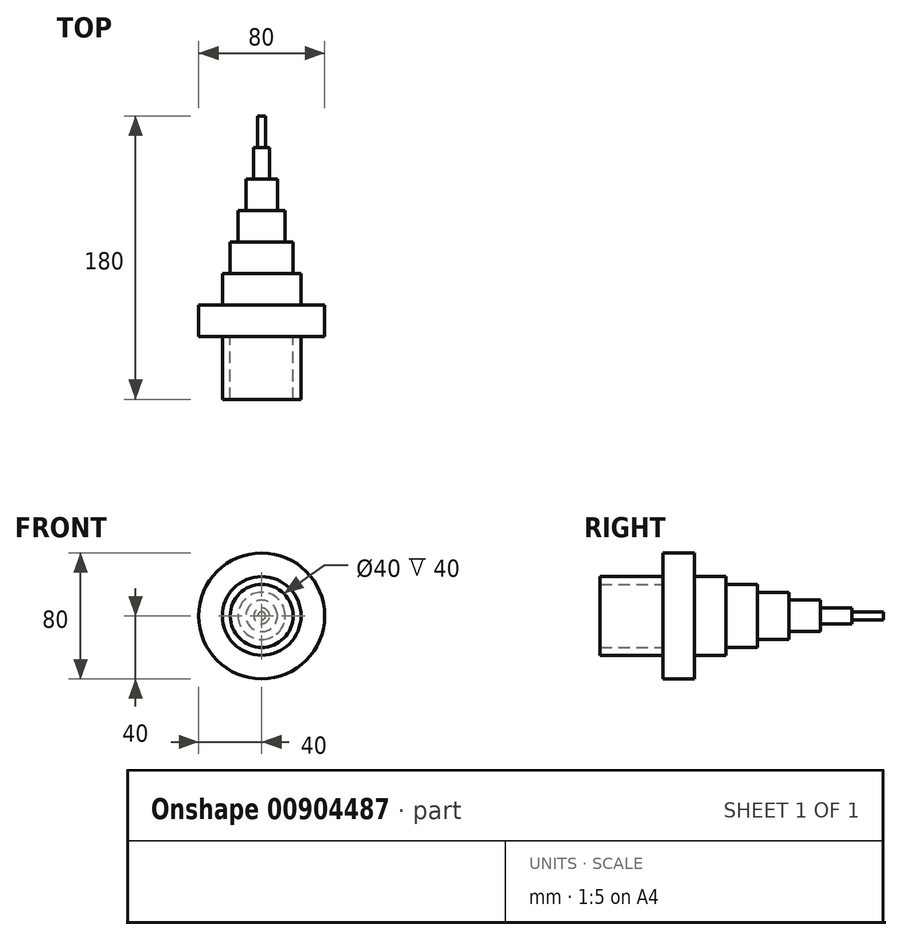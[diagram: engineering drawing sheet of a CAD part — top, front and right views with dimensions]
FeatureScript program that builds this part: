
annotation { "Feature Type Name" : "Feature", "Feature Type Description" : "" }
export const myFeature = defineFeature(function(context is Context, id is Id, definition is map)
    precondition{}
    {
        {
            var Q0;
            Q0=qCreatedBy(makeId("Front.planeOp"),FACE);
            var sketch = newSketch(context, id + "F0", { "sketchPlane" : qUnion([Q0])});
            skCircle(sketch, "E0", {"center": v(0, 0) * mm, "radius": 40 * mm});
            skSolve(sketch);
        }
        {
            var Q0;
            Q0=makeQuery(id+"F0.imprint","IMPRINT",FACE,{"disambiguationData":[TD([[makeQuery(id+"F0.imprint","IMPRINT",EDGE,{"derivedFrom":sQuery(id+"F0.wireOp",EDGE,"E0")}),1.0]])]});
            extrude(context, id + "F1", {"entities" : qUnion([Q0]), "depth" : 20 * mm, "offsetDistance" : 25.4 * mm});
        }
        {
            var Q0;
            Q0=makeQuery(id+"F1.opExtrude","CAP_FACE",FACE,{"disambiguationData":[OSD([sQuery(id+"F0.wireOp",EDGE,"E0")])],"isStart":false});
            var sketch = newSketch(context, id + "F2", { "sketchPlane" : qUnion([Q0])});
            skCircle(sketch, "E1", {"center": v(0, 0) * mm, "radius": 25 * mm});
            skCircle(sketch, "E2", {"center": v(0, 0) * mm, "radius": 20 * mm});
            skSolve(sketch);
        }
        {
            var Q0;
            Q0 = qSketchRegion(id + "F2", true);
            extrude(context, id + "F3", {"entities" : qUnion([Q0]), "operationType" : NewBodyOperationType.ADD, "depth" : 40 * mm, "offsetDistance" : 25.4 * mm});
        }
        {
            var Q0;
            Q0=makeQuery(id+"F1.opExtrude","CAP_FACE",FACE,{"disambiguationData":[OSD([sQuery(id+"F0.wireOp",EDGE,"E0")])],"isStart":true});
            var sketch = newSketch(context, id + "F4", { "sketchPlane" : qUnion([Q0])});
            skCircle(sketch, "E3", {"center": v(0, 0) * mm, "radius": 25 * mm});
            skCircle(sketch, "E4", {"center": v(0, 0) * mm, "radius": 20 * mm});
            skCircle(sketch, "E5", {"center": v(0, 0) * mm, "radius": 15 * mm});
            skCircle(sketch, "E6", {"center": v(0, 0) * mm, "radius": 10 * mm});
            skCircle(sketch, "E7", {"center": v(0, 0) * mm, "radius": 5 * mm});
            skCircle(sketch, "E8", {"center": v(0, 0) * mm, "radius": 2.5 * mm});
            skSolve(sketch);
        }
        {
            var Q0;
            Q0=makeQuery(id+"F4.imprint","IMPRINT",FACE,{"disambiguationData":[TD([[makeQuery(id+"F4.imprint","IMPRINT",EDGE,{"derivedFrom":sQuery(id+"F4.wireOp",EDGE,"E3")}),1.0]])]});
            extrude(context, id + "F5", {"entities" : qUnion([Q0]), "operationType" : NewBodyOperationType.ADD, "depth" : 20 * mm, "offsetDistance" : 25.4 * mm});
        }
        {
            var Q0;
            Q0=makeQuery(id+"F5.boolean.opBoolean","SPLIT",FACE,{"disambiguationData":[TD([makeQuery(id+"F5.opExtrude","SWEPT_FACE",FACE,{"disambiguationData":[OSD([sQuery(id+"F4.wireOp",EDGE,"E4")])]})])],"derivedFrom":makeQuery(id+"F1.opExtrude","CAP_FACE",FACE,{"disambiguationData":[OSD([sQuery(id+"F0.wireOp",EDGE,"E0")])],"isStart":true})});
            extrude(context, id + "F6", {"entities" : qUnion([Q0]), "operationType" : NewBodyOperationType.ADD, "depth" : 40 * mm, "offsetDistance" : 25.4 * mm});
        }
        {
            var Q0;
            Q0=makeQuery(id+"F6.opExtrude","CAP_FACE",FACE,{"disambiguationData":[OSD([sQuery(id+"F0.wireOp",EDGE,"E0")])],"isStart":false});
            var sketch = newSketch(context, id + "F7", { "sketchPlane" : qUnion([Q0])});
            skCircle(sketch, "E9", {"center": v(0, 0) * mm, "radius": 2.5 * mm});
            skSolve(sketch);
        }
        {
            var Q0;
            Q0=makeQuery(id+"F7.imprint","IMPRINT",FACE,{"disambiguationData":[TD([[makeQuery(id+"F7.imprint","IMPRINT",EDGE,{"derivedFrom":sQuery(id+"F7.wireOp",EDGE,"E9")}),1.0]])]});
            extrude(context, id + "F8", {"entities" : qUnion([Q0]), "operationType" : NewBodyOperationType.ADD, "depth" : 80 * mm, "offsetDistance" : 25.4 * mm});
        }
        {
            var Q0;
            Q0=makeQuery(id+"F6.opExtrude","CAP_FACE",FACE,{"disambiguationData":[OSD([sQuery(id+"F0.wireOp",EDGE,"E0")])],"isStart":false});
            var sketch = newSketch(context, id + "F9", { "sketchPlane" : qUnion([Q0])});
            skCircle(sketch, "E10", {"center": v(0, 0) * mm, "radius": 15 * mm});
            skSolve(sketch);
        }
        {
            var Q0;
            Q0=makeQuery(id+"F9.imprint","IMPRINT",FACE,{"disambiguationData":[TD([[makeQuery(id+"F9.imprint","IMPRINT",EDGE,{"derivedFrom":sQuery(id+"F9.wireOp",EDGE,"E10")}),1.0]])]});
            extrude(context, id + "F10", {"entities" : qUnion([Q0]), "operationType" : NewBodyOperationType.ADD, "depth" : 20 * mm, "offsetDistance" : 25.4 * mm});
        }
        {
            var Q0;
            Q0=makeQuery(id+"F10.opExtrude","CAP_FACE",FACE,{"disambiguationData":[OSD([sQuery(id+"F7.wireOp",EDGE,"E9"),sQuery(id+"F9.wireOp",EDGE,"E10")])],"isStart":false});
            var sketch = newSketch(context, id + "F11", { "sketchPlane" : qUnion([Q0])});
            skCircle(sketch, "E11", {"center": v(0, 0) * mm, "radius": 10 * mm});
            skCircle(sketch, "E12", {"center": v(0, 0) * mm, "radius": 5 * mm});
            skSolve(sketch);
        }
        {
            var Q0;
            Q0=makeQuery(id+"F11.imprint","IMPRINT",FACE,{"disambiguationData":[TD([[makeQuery(id+"F11.imprint","IMPRINT",EDGE,{"derivedFrom":sQuery(id+"F11.wireOp",EDGE,"E12")}),1.0]])]});
            extrude(context, id + "F12", {"entities" : qUnion([Q0]), "operationType" : NewBodyOperationType.ADD, "depth" : 40 * mm, "offsetDistance" : 25.4 * mm});
        }
        {
            var Q0;
            Q0=makeQuery(id+"F10.opExtrude","CAP_FACE",FACE,{"disambiguationData":[OSD([sQuery(id+"F7.wireOp",EDGE,"E9"),sQuery(id+"F9.wireOp",EDGE,"E10")])],"isStart":false});
            var sketch = newSketch(context, id + "F13", { "sketchPlane" : qUnion([Q0])});
            skCircle(sketch, "E13", {"center": v(0, 0) * mm, "radius": 10 * mm});
            skSolve(sketch);
        }
        {
            var Q0;
            Q0=makeQuery(id+"F13.imprint","IMPRINT",FACE,{"disambiguationData":[TD([[makeQuery(id+"F13.imprint","IMPRINT",EDGE,{"derivedFrom":sQuery(id+"F13.wireOp",EDGE,"E13")}),1.0]])]});
            extrude(context, id + "F14", {"entities" : qUnion([Q0]), "operationType" : NewBodyOperationType.ADD, "depth" : 20 * mm, "offsetDistance" : 25.4 * mm});
        }
    });
